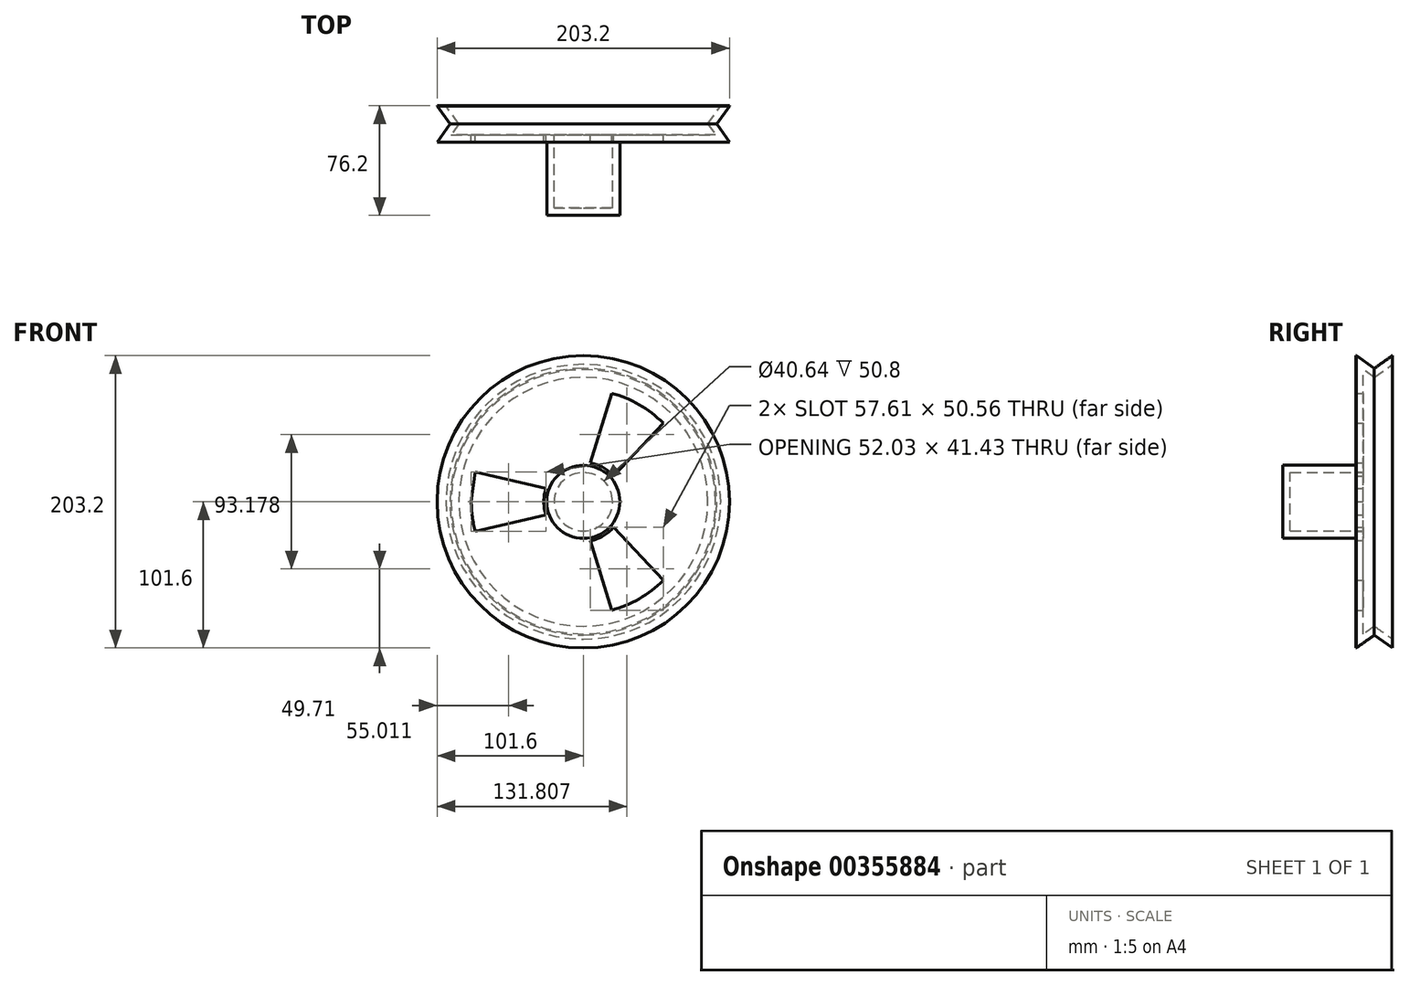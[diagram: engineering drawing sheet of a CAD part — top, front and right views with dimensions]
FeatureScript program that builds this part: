
annotation { "Feature Type Name" : "Feature", "Feature Type Description" : "" }
export const myFeature = defineFeature(function(context is Context, id is Id, definition is map)
    precondition{}
    {
        {
            var Q0;
            Q0=qCreatedBy(makeId("Front.planeOp"),FACE);
            var sketch = newSketch(context, id + "F0", { "sketchPlane" : qUnion([Q0])});
            skCircle(sketch, "E0", {"center": v(0, 0) * mm, "radius": 101.6 * mm});
            skSolve(sketch);
        }
        {
            var Q0;
            Q0=makeQuery(id+"F0.imprint","IMPRINT",FACE,{"disambiguationData":[TD([[makeQuery(id+"F0.imprint","IMPRINT",EDGE,{"derivedFrom":sQuery(id+"F0.wireOp",EDGE,"E0")}),1.0]])]});
            extrude(context, id + "F1", {"entities" : qUnion([Q0]), "depth" : 25.4 * mm});
        }
        {
            var Q0;
            Q0=qCreatedBy(makeId("Right.planeOp"),FACE);
            var sketch = newSketch(context, id + "F2", { "sketchPlane" : qUnion([Q0])});
            skLineSegment(sketch, "E1", {"start": v(0, 101.7) * mm, "end": v(-12.7, 101.7) * mm});
            skLineSegment(sketch, "E2", {"start": v(0, 101.7) * mm, "end": v(-12.7, 92.73) * mm});
            skLineSegment(sketch, "E3", {"start": v(-12.7, 92.73) * mm, "end": v(-25.44, 101.7) * mm});
            skLineSegment(sketch, "E4", {"start": v(-25.44, 101.7) * mm, "end": v(-12.7, 101.7) * mm});
            skSolve(sketch);
        }
        {
            var Q0;
            Q0=qSketchRegion(id+"F2",true);
            var Q1;
            Q1=makeQuery(id+"F1.opExtrude","CAP_EDGE",EDGE,{"disambiguationData":[OSD([sQuery(id+"F0.wireOp",EDGE,"E0")])],"isStart":false});
            revolve(context, id + "F3", {"operationType" : NewBodyOperationType.REMOVE, "entities" : qUnion([Q0]), "axis" : qUnion([Q1]), "revolveType" : RevolveType.FULL, "oppositeDirection" : true});
        }
        {
            var Q0;
            Q0=makeQuery(id+"F1.opExtrude","CAP_FACE",FACE,{"disambiguationData":[OSD([sQuery(id+"F0.wireOp",EDGE,"E0")])],"isStart":false});
            var sketch = newSketch(context, id + "F4", { "sketchPlane" : qUnion([Q0])});
            skCircle(sketch, "E5", {"center": v(0, 0) * mm, "radius": 25.4 * mm});
            skSolve(sketch);
        }
        {
            var Q0;
            Q0=qSketchRegion(id+"F4",true);
            extrude(context, id + "F5", {"entities" : qUnion([Q0]), "operationType" : NewBodyOperationType.ADD, "depth" : 50.8 * mm});
        }
        {
            var Q0;
            Q0=makeQuery(id+"F1.opExtrude","CAP_FACE",FACE,{"disambiguationData":[OSD([sQuery(id+"F0.wireOp",EDGE,"E0")])],"isStart":true});
            shell(context, id + "F6", {"entities" : qUnion([Q0]), "thickness" : 5.08 * mm});
        }
        {
            var Q0;
            Q0=makeQuery(id+"F6.opShell","OFFSET_FACE",FACE,{"disambiguationData":[OSD([sQuery(id+"F0.wireOp",EDGE,"E0")])]});
            var sketch = newSketch(context, id + "F7", { "sketchPlane" : qUnion([Q0])});
            skCircle(sketch, "E6", {"center": v(0, 0) * mm, "radius": 77.9 * mm});
            skCircle(sketch, "E7", {"center": v(0, 0) * mm, "radius": 27.48 * mm});
            skLineSegment(sketch, "E8", {"start": v(77.9, 0) * mm, "end": v(75.1, 20.71) * mm});
            skLineSegment(sketch, "E9", {"start": v(75.1, 20.71) * mm, "end": v(25.88, 9.25) * mm});
            skLineSegment(sketch, "E10.MirrorCS", {"start": v(75.1, -20.71) * mm, "end": v(25.88, -9.25) * mm});
            skPoint(sketch, "E11.start.orphan", {"position": v(27.48, 0) * mm});
            skLineSegment(sketch, "E12.1.0", {"start": v(-19.61, 75.4) * mm, "end": v(-4.93, 27.04) * mm});
            skLineSegment(sketch, "E12.1.1", {"start": v(-55.49, 54.68) * mm, "end": v(-20.95, 17.78) * mm});
            skLineSegment(sketch, "E12.2.0", {"start": v(-55.49, -54.68) * mm, "end": v(-20.95, -17.78) * mm});
            skLineSegment(sketch, "E12.2.1", {"start": v(-19.61, -75.4) * mm, "end": v(-4.93, -27.04) * mm});
            skSolve(sketch);
        }
        {
            var Q0;
            {var subQ0=sQuery(id+"F7.wireOp",EDGE,"E12.1.0");Q0=makeQuery(id+"F7.imprint","IMPRINT",FACE,{"disambiguationData":[TD([[makeQuery(id+"F7.imprint","IMPRINT",EDGE,{"derivedFrom":subQ0}),-1.0]])]});}
            var Q1;
            {var subQ0=sQuery(id+"F7.wireOp",EDGE,"E12.2.0");Q1=makeQuery(id+"F7.imprint","IMPRINT",FACE,{"disambiguationData":[TD([[makeQuery(id+"F7.imprint","IMPRINT",EDGE,{"derivedFrom":subQ0}),-1.0]])]});}
            var Q2;
            {var subQ1=sQuery(id+"F7.wireOp",EDGE,"E8");Q2=makeQuery(id+"F7.imprint","IMPRINT",FACE,{"disambiguationData":[TD([[makeQuery(id+"F7.imprint","IMPRINT",EDGE,{"derivedFrom":subQ1}),1.0]])]});}
            extrude(context, id + "F8", {"entities" : qUnion([Q0, Q1, Q2]), "operationType" : NewBodyOperationType.REMOVE, "endBound" : BoundingType.THROUGH_ALL, "oppositeDirection" : true, "depth" : 25.4 * mm});
        }
    });
